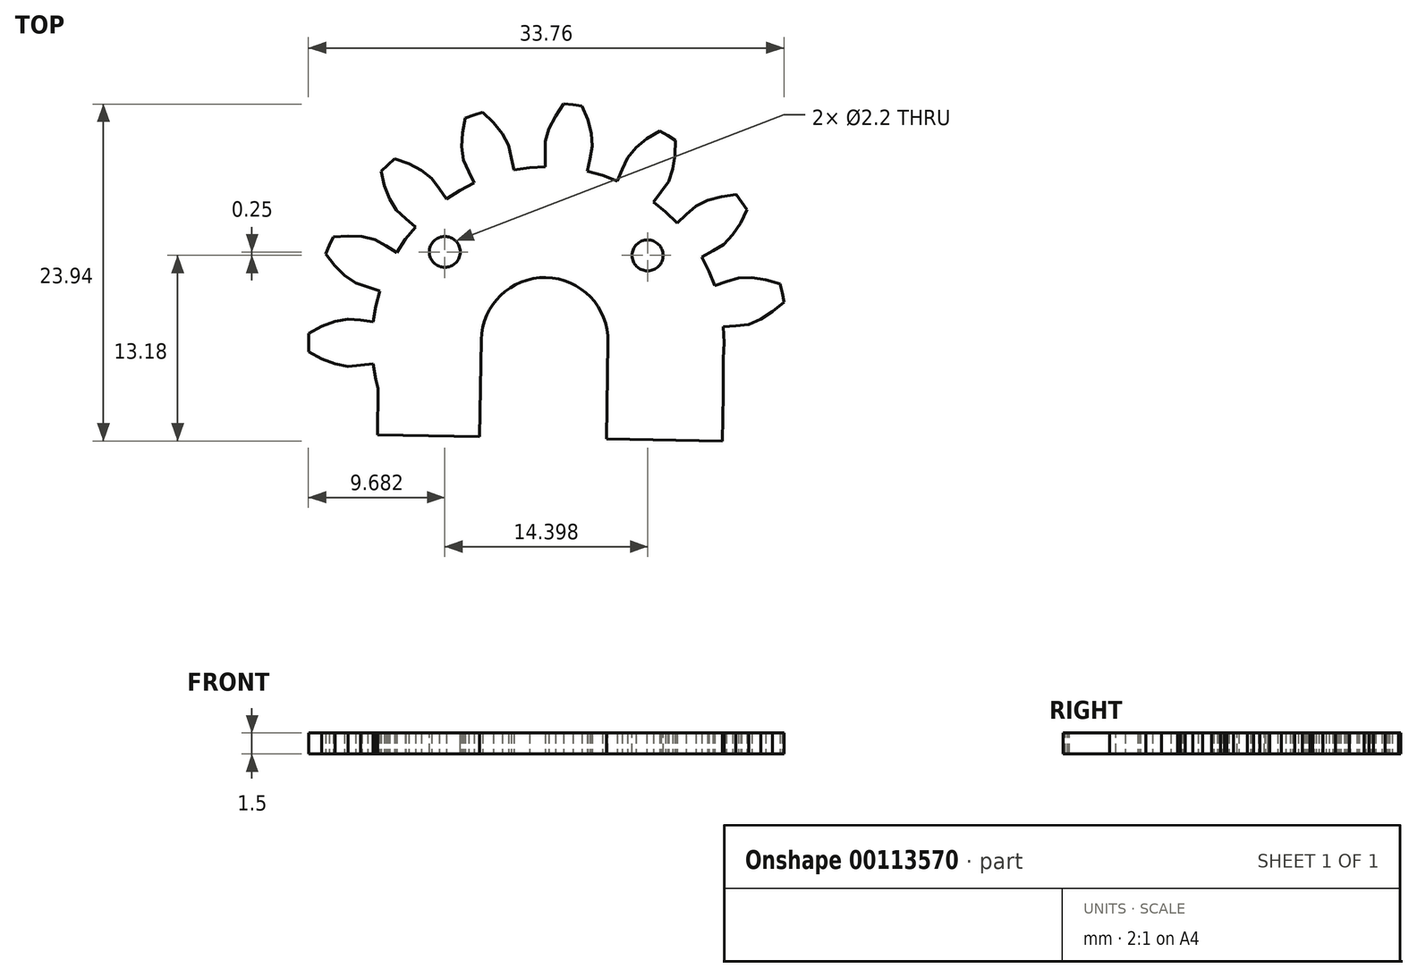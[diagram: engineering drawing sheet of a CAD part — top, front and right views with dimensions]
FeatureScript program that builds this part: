
annotation { "Feature Type Name" : "Feature", "Feature Type Description" : "" }
export const myFeature = defineFeature(function(context is Context, id is Id, definition is map)
    precondition{}
    {
        {
            var Q0;
            Q0=qCreatedBy(makeId("Top.planeOp"),FACE);
            var sketch = newSketch(context, id + "F0", { "sketchPlane" : qUnion([Q0])});
            skLineSegment(sketch, "E0", {"start": v(12.62, 0) * mm, "end": v(12.57, 1.12) * mm});
            skLineSegment(sketch, "E1", {"start": v(12.57, 1.12) * mm, "end": v(13.47, 1.2) * mm});
            skLineSegment(sketch, "E2", {"start": v(13.47, 1.2) * mm, "end": v(14.36, 1.3) * mm});
            skLineSegment(sketch, "E3", {"start": v(14.36, 1.3) * mm, "end": v(15.23, 1.67) * mm});
            skLineSegment(sketch, "E4", {"start": v(15.23, 1.67) * mm, "end": v(16.07, 2.2) * mm});
            skLineSegment(sketch, "E5", {"start": v(16.07, 2.2) * mm, "end": v(16.88, 2.89) * mm});
            skLineSegment(sketch, "E6", {"start": v(16.88, 2.89) * mm, "end": v(16.75, 3.53) * mm});
            skLineSegment(sketch, "E7", {"start": v(16.75, 3.53) * mm, "end": v(16.6, 4.17) * mm});
            skLineSegment(sketch, "E8", {"start": v(16.6, 4.17) * mm, "end": v(15.6, 4.47) * mm});
            skLineSegment(sketch, "E9", {"start": v(15.6, 4.47) * mm, "end": v(14.6, 4.62) * mm});
            skLineSegment(sketch, "E10", {"start": v(14.6, 4.62) * mm, "end": v(13.66, 4.6) * mm});
            skLineSegment(sketch, "E11", {"start": v(13.66, 4.6) * mm, "end": v(12.8, 4.33) * mm});
            skLineSegment(sketch, "E12", {"start": v(12.8, 4.33) * mm, "end": v(11.95, 4.04) * mm});
            skLineSegment(sketch, "E13", {"start": v(11.95, 4.04) * mm, "end": v(11.54, 5.08) * mm});
            skLineSegment(sketch, "E14", {"start": v(11.54, 5.08) * mm, "end": v(11.04, 6.09) * mm});
            skLineSegment(sketch, "E15", {"start": v(11.04, 6.09) * mm, "end": v(11.83, 6.53) * mm});
            skLineSegment(sketch, "E16", {"start": v(11.83, 6.53) * mm, "end": v(12.6, 6.99) * mm});
            skLineSegment(sketch, "E17", {"start": v(12.6, 6.99) * mm, "end": v(13.25, 7.67) * mm});
            skLineSegment(sketch, "E18", {"start": v(13.25, 7.67) * mm, "end": v(13.8, 8.5) * mm});
            skLineSegment(sketch, "E19", {"start": v(13.8, 8.5) * mm, "end": v(14.25, 9.45) * mm});
            skLineSegment(sketch, "E20", {"start": v(14.25, 9.45) * mm, "end": v(13.88, 10) * mm});
            skLineSegment(sketch, "E21", {"start": v(13.88, 10) * mm, "end": v(13.48, 10.52) * mm});
            skLineSegment(sketch, "E22", {"start": v(13.48, 10.52) * mm, "end": v(12.43, 10.38) * mm});
            skLineSegment(sketch, "E23", {"start": v(12.43, 10.38) * mm, "end": v(11.47, 10.11) * mm});
            skLineSegment(sketch, "E24", {"start": v(11.47, 10.11) * mm, "end": v(10.62, 9.7) * mm});
            skLineSegment(sketch, "E25", {"start": v(10.62, 9.7) * mm, "end": v(9.95, 9.11) * mm});
            skLineSegment(sketch, "E26", {"start": v(9.95, 9.11) * mm, "end": v(9.29, 8.5) * mm});
            skLineSegment(sketch, "E27", {"start": v(9.29, 8.5) * mm, "end": v(8.49, 9.29) * mm});
            skLineSegment(sketch, "E28", {"start": v(8.49, 9.29) * mm, "end": v(7.62, 10) * mm});
            skLineSegment(sketch, "E29", {"start": v(7.62, 10) * mm, "end": v(8.16, 10.72) * mm});
            skLineSegment(sketch, "E30", {"start": v(8.16, 10.72) * mm, "end": v(8.68, 11.46) * mm});
            skLineSegment(sketch, "E31", {"start": v(8.68, 11.46) * mm, "end": v(9, 12.34) * mm});
            skLineSegment(sketch, "E32", {"start": v(9, 12.34) * mm, "end": v(9.16, 13.33) * mm});
            skLineSegment(sketch, "E33", {"start": v(9.16, 13.33) * mm, "end": v(9.19, 14.38) * mm});
            skLineSegment(sketch, "E34", {"start": v(9.19, 14.38) * mm, "end": v(8.62, 14.72) * mm});
            skLineSegment(sketch, "E35", {"start": v(8.62, 14.72) * mm, "end": v(8.05, 15.04) * mm});
            skLineSegment(sketch, "E36", {"start": v(8.05, 15.04) * mm, "end": v(7.15, 14.49) * mm});
            skLineSegment(sketch, "E37", {"start": v(7.15, 14.49) * mm, "end": v(6.38, 13.85) * mm});
            skLineSegment(sketch, "E38", {"start": v(6.38, 13.85) * mm, "end": v(5.77, 13.14) * mm});
            skLineSegment(sketch, "E39", {"start": v(5.77, 13.14) * mm, "end": v(5.4, 12.32) * mm});
            skLineSegment(sketch, "E40", {"start": v(5.4, 12.32) * mm, "end": v(5.04, 11.5) * mm});
            skLineSegment(sketch, "E41", {"start": v(5.04, 11.5) * mm, "end": v(3.99, 11.89) * mm});
            skLineSegment(sketch, "E42", {"start": v(3.99, 11.89) * mm, "end": v(2.9, 12.19) * mm});
            skLineSegment(sketch, "E43", {"start": v(2.9, 12.19) * mm, "end": v(3.1, 13.06) * mm});
            skLineSegment(sketch, "E44", {"start": v(3.1, 13.06) * mm, "end": v(3.28, 13.95) * mm});
            skLineSegment(sketch, "E45", {"start": v(3.28, 13.95) * mm, "end": v(3.2, 14.88) * mm});
            skLineSegment(sketch, "E46", {"start": v(3.2, 14.88) * mm, "end": v(2.95, 15.85) * mm});
            skLineSegment(sketch, "E47", {"start": v(2.95, 15.85) * mm, "end": v(2.55, 16.83) * mm});
            skLineSegment(sketch, "E48", {"start": v(2.55, 16.83) * mm, "end": v(1.9, 16.9) * mm});
            skLineSegment(sketch, "E49", {"start": v(1.9, 16.9) * mm, "end": v(1.25, 16.96) * mm});
            skLineSegment(sketch, "E50", {"start": v(1.25, 16.96) * mm, "end": v(0.65, 16.1) * mm});
            skLineSegment(sketch, "E51", {"start": v(0.65, 16.1) * mm, "end": v(0.2, 15.2) * mm});
            skLineSegment(sketch, "E52", {"start": v(0.2, 15.2) * mm, "end": v(-0.07, 14.3) * mm});
            skLineSegment(sketch, "E53", {"start": v(-0.07, 14.3) * mm, "end": v(-0.08, 13.4) * mm});
            skLineSegment(sketch, "E54", {"start": v(-0.08, 13.4) * mm, "end": v(-0.06, 12.5) * mm});
            skLineSegment(sketch, "E55", {"start": v(-0.06, 12.5) * mm, "end": v(-1.18, 12.43) * mm});
            skLineSegment(sketch, "E56", {"start": v(-1.18, 12.43) * mm, "end": v(-2.3, 12.26) * mm});
            skLineSegment(sketch, "E57", {"start": v(-2.3, 12.26) * mm, "end": v(-2.47, 13.15) * mm});
            skLineSegment(sketch, "E58", {"start": v(-2.47, 13.15) * mm, "end": v(-2.66, 14.03) * mm});
            skLineSegment(sketch, "E59", {"start": v(-2.66, 14.03) * mm, "end": v(-3.11, 14.85) * mm});
            skLineSegment(sketch, "E60", {"start": v(-3.11, 14.85) * mm, "end": v(-3.74, 15.63) * mm});
            skLineSegment(sketch, "E61", {"start": v(-3.74, 15.63) * mm, "end": v(-4.5, 16.36) * mm});
            skLineSegment(sketch, "E62", {"start": v(-4.5, 16.36) * mm, "end": v(-5.13, 16.17) * mm});
            skLineSegment(sketch, "E63", {"start": v(-5.13, 16.17) * mm, "end": v(-5.75, 15.95) * mm});
            skLineSegment(sketch, "E64", {"start": v(-5.75, 15.95) * mm, "end": v(-5.94, 14.91) * mm});
            skLineSegment(sketch, "E65", {"start": v(-5.94, 14.91) * mm, "end": v(-5.99, 13.92) * mm});
            skLineSegment(sketch, "E66", {"start": v(-5.99, 13.92) * mm, "end": v(-5.87, 12.99) * mm});
            skLineSegment(sketch, "E67", {"start": v(-5.87, 12.99) * mm, "end": v(-5.5, 12.16) * mm});
            skLineSegment(sketch, "E68", {"start": v(-5.5, 12.16) * mm, "end": v(-5.13, 11.34) * mm});
            skLineSegment(sketch, "E69", {"start": v(-5.13, 11.34) * mm, "end": v(-6.13, 10.83) * mm});
            skLineSegment(sketch, "E70", {"start": v(-6.13, 10.83) * mm, "end": v(-7.07, 10.22) * mm});
            skLineSegment(sketch, "E71", {"start": v(-7.07, 10.22) * mm, "end": v(-7.6, 10.96) * mm});
            skLineSegment(sketch, "E72", {"start": v(-7.6, 10.96) * mm, "end": v(-8.13, 11.68) * mm});
            skLineSegment(sketch, "E73", {"start": v(-8.13, 11.68) * mm, "end": v(-8.87, 12.25) * mm});
            skLineSegment(sketch, "E74", {"start": v(-8.87, 12.25) * mm, "end": v(-9.76, 12.7) * mm});
            skLineSegment(sketch, "E75", {"start": v(-9.76, 12.7) * mm, "end": v(-10.76, 13.06) * mm});
            skLineSegment(sketch, "E76", {"start": v(-10.76, 13.06) * mm, "end": v(-11.25, 12.63) * mm});
            skLineSegment(sketch, "E77", {"start": v(-11.25, 12.63) * mm, "end": v(-11.73, 12.18) * mm});
            skLineSegment(sketch, "E78", {"start": v(-11.73, 12.18) * mm, "end": v(-11.48, 11.16) * mm});
            skLineSegment(sketch, "E79", {"start": v(-11.48, 11.16) * mm, "end": v(-11.12, 10.23) * mm});
            skLineSegment(sketch, "E80", {"start": v(-11.12, 10.23) * mm, "end": v(-10.63, 9.43) * mm});
            skLineSegment(sketch, "E81", {"start": v(-10.63, 9.43) * mm, "end": v(-9.97, 8.82) * mm});
            skLineSegment(sketch, "E82", {"start": v(-9.97, 8.82) * mm, "end": v(-9.29, 8.22) * mm});
            skLineSegment(sketch, "E83", {"start": v(-9.29, 8.22) * mm, "end": v(-9.99, 7.35) * mm});
            skLineSegment(sketch, "E84", {"start": v(-9.99, 7.35) * mm, "end": v(-10.6, 6.41) * mm});
            skLineSegment(sketch, "E85", {"start": v(-10.6, 6.41) * mm, "end": v(-11.38, 6.87) * mm});
            skLineSegment(sketch, "E86", {"start": v(-11.38, 6.87) * mm, "end": v(-12.16, 7.31) * mm});
            skLineSegment(sketch, "E87", {"start": v(-12.16, 7.31) * mm, "end": v(-13.08, 7.53) * mm});
            skLineSegment(sketch, "E88", {"start": v(-13.08, 7.53) * mm, "end": v(-14.08, 7.59) * mm});
            skLineSegment(sketch, "E89", {"start": v(-14.08, 7.59) * mm, "end": v(-15.13, 7.5) * mm});
            skLineSegment(sketch, "E90", {"start": v(-15.13, 7.5) * mm, "end": v(-15.4, 6.91) * mm});
            skLineSegment(sketch, "E91", {"start": v(-15.4, 6.91) * mm, "end": v(-15.66, 6.3) * mm});
            skLineSegment(sketch, "E92", {"start": v(-15.66, 6.3) * mm, "end": v(-15.02, 5.47) * mm});
            skLineSegment(sketch, "E93", {"start": v(-15.02, 5.47) * mm, "end": v(-14.3, 4.77) * mm});
            skLineSegment(sketch, "E94", {"start": v(-14.3, 4.77) * mm, "end": v(-13.53, 4.24) * mm});
            skLineSegment(sketch, "E95", {"start": v(-13.53, 4.24) * mm, "end": v(-12.68, 3.95) * mm});
            skLineSegment(sketch, "E96", {"start": v(-12.68, 3.95) * mm, "end": v(-11.82, 3.69) * mm});
            skLineSegment(sketch, "E97", {"start": v(-11.82, 3.69) * mm, "end": v(-12.1, 2.6) * mm});
            skLineSegment(sketch, "E98", {"start": v(-12.1, 2.6) * mm, "end": v(-12.29, 1.5) * mm});
            skLineSegment(sketch, "E99", {"start": v(-12.29, 1.5) * mm, "end": v(-13.18, 1.6) * mm});
            skLineSegment(sketch, "E100", {"start": v(-13.18, 1.6) * mm, "end": v(-14.08, 1.68) * mm});
            skLineSegment(sketch, "E101", {"start": v(-14.08, 1.68) * mm, "end": v(-15, 1.51) * mm});
            skLineSegment(sketch, "E102", {"start": v(-15, 1.51) * mm, "end": v(-15.93, 1.16) * mm});
            skLineSegment(sketch, "E103", {"start": v(-15.93, 1.16) * mm, "end": v(-16.86, 0.66) * mm});
            skLineSegment(sketch, "E104", {"start": v(-16.86, 0.66) * mm, "end": v(-16.88, 0) * mm});
            skLineSegment(sketch, "E105", {"start": v(-16.88, 0) * mm, "end": v(-16.86, -0.66) * mm});
            skLineSegment(sketch, "E106", {"start": v(-16.86, -0.66) * mm, "end": v(-15.93, -1.16) * mm});
            skLineSegment(sketch, "E107", {"start": v(-15.93, -1.16) * mm, "end": v(-15, -1.51) * mm});
            skLineSegment(sketch, "E108", {"start": v(-15, -1.51) * mm, "end": v(-14.08, -1.68) * mm});
            skLineSegment(sketch, "E109", {"start": v(-14.08, -1.68) * mm, "end": v(-13.18, -1.6) * mm});
            skLineSegment(sketch, "E110", {"start": v(-13.18, -1.6) * mm, "end": v(-12.29, -1.5) * mm});
            skLineSegment(sketch, "E111", {"start": v(-12.29, -1.5) * mm, "end": v(-12.1, -2.6) * mm});
            skLineSegment(sketch, "E112", {"start": v(-12.1, -2.6) * mm, "end": v(-11.82, -3.69) * mm});
            skLineSegment(sketch, "E113", {"start": v(-11.82, -3.69) * mm, "end": v(-12.68, -3.95) * mm});
            skLineSegment(sketch, "E114", {"start": v(-12.68, -3.95) * mm, "end": v(-13.53, -4.24) * mm});
            skLineSegment(sketch, "E115", {"start": v(-13.53, -4.24) * mm, "end": v(-14.3, -4.77) * mm});
            skLineSegment(sketch, "E116", {"start": v(-14.3, -4.77) * mm, "end": v(-15.02, -5.47) * mm});
            skLineSegment(sketch, "E117", {"start": v(-15.02, -5.47) * mm, "end": v(-15.66, -6.3) * mm});
            skLineSegment(sketch, "E118", {"start": v(-15.66, -6.3) * mm, "end": v(-15.4, -6.91) * mm});
            skLineSegment(sketch, "E119", {"start": v(-15.4, -6.91) * mm, "end": v(-15.13, -7.5) * mm});
            skLineSegment(sketch, "E120", {"start": v(-15.13, -7.5) * mm, "end": v(-14.08, -7.59) * mm});
            skLineSegment(sketch, "E121", {"start": v(-14.08, -7.59) * mm, "end": v(-13.08, -7.53) * mm});
            skLineSegment(sketch, "E122", {"start": v(-13.08, -7.53) * mm, "end": v(-12.16, -7.31) * mm});
            skLineSegment(sketch, "E123", {"start": v(-12.16, -7.31) * mm, "end": v(-11.38, -6.87) * mm});
            skLineSegment(sketch, "E124", {"start": v(-11.38, -6.87) * mm, "end": v(-10.6, -6.41) * mm});
            skLineSegment(sketch, "E125", {"start": v(-10.6, -6.41) * mm, "end": v(-9.99, -7.35) * mm});
            skLineSegment(sketch, "E126", {"start": v(-9.99, -7.35) * mm, "end": v(-9.29, -8.22) * mm});
            skLineSegment(sketch, "E127", {"start": v(-9.29, -8.22) * mm, "end": v(-9.97, -8.82) * mm});
            skLineSegment(sketch, "E128", {"start": v(-9.97, -8.82) * mm, "end": v(-10.63, -9.43) * mm});
            skLineSegment(sketch, "E129", {"start": v(-10.63, -9.43) * mm, "end": v(-11.12, -10.23) * mm});
            skLineSegment(sketch, "E130", {"start": v(-11.12, -10.23) * mm, "end": v(-11.48, -11.16) * mm});
            skLineSegment(sketch, "E131", {"start": v(-11.48, -11.16) * mm, "end": v(-11.73, -12.18) * mm});
            skLineSegment(sketch, "E132", {"start": v(-11.73, -12.18) * mm, "end": v(-11.25, -12.63) * mm});
            skLineSegment(sketch, "E133", {"start": v(-11.25, -12.63) * mm, "end": v(-10.76, -13.06) * mm});
            skLineSegment(sketch, "E134", {"start": v(-10.76, -13.06) * mm, "end": v(-9.76, -12.7) * mm});
            skLineSegment(sketch, "E135", {"start": v(-9.76, -12.7) * mm, "end": v(-8.87, -12.25) * mm});
            skLineSegment(sketch, "E136", {"start": v(-8.87, -12.25) * mm, "end": v(-8.13, -11.68) * mm});
            skLineSegment(sketch, "E137", {"start": v(-8.13, -11.68) * mm, "end": v(-7.6, -10.96) * mm});
            skLineSegment(sketch, "E138", {"start": v(-7.6, -10.96) * mm, "end": v(-7.07, -10.22) * mm});
            skLineSegment(sketch, "E139", {"start": v(-7.07, -10.22) * mm, "end": v(-6.13, -10.83) * mm});
            skLineSegment(sketch, "E140", {"start": v(-6.13, -10.83) * mm, "end": v(-5.13, -11.34) * mm});
            skLineSegment(sketch, "E141", {"start": v(-5.13, -11.34) * mm, "end": v(-5.5, -12.16) * mm});
            skLineSegment(sketch, "E142", {"start": v(-5.5, -12.16) * mm, "end": v(-5.87, -12.99) * mm});
            skLineSegment(sketch, "E143", {"start": v(-5.87, -12.99) * mm, "end": v(-5.99, -13.92) * mm});
            skLineSegment(sketch, "E144", {"start": v(-5.99, -13.92) * mm, "end": v(-5.94, -14.91) * mm});
            skLineSegment(sketch, "E145", {"start": v(-5.94, -14.91) * mm, "end": v(-5.75, -15.95) * mm});
            skLineSegment(sketch, "E146", {"start": v(-5.75, -15.95) * mm, "end": v(-5.13, -16.17) * mm});
            skLineSegment(sketch, "E147", {"start": v(-5.13, -16.17) * mm, "end": v(-4.5, -16.36) * mm});
            skLineSegment(sketch, "E148", {"start": v(-4.5, -16.36) * mm, "end": v(-3.74, -15.63) * mm});
            skLineSegment(sketch, "E149", {"start": v(-3.74, -15.63) * mm, "end": v(-3.11, -14.85) * mm});
            skLineSegment(sketch, "E150", {"start": v(-3.11, -14.85) * mm, "end": v(-2.66, -14.03) * mm});
            skLineSegment(sketch, "E151", {"start": v(-2.66, -14.03) * mm, "end": v(-2.47, -13.15) * mm});
            skLineSegment(sketch, "E152", {"start": v(-2.47, -13.15) * mm, "end": v(-2.3, -12.26) * mm});
            skLineSegment(sketch, "E153", {"start": v(-2.3, -12.26) * mm, "end": v(-1.18, -12.43) * mm});
            skLineSegment(sketch, "E154", {"start": v(-1.18, -12.43) * mm, "end": v(-0.06, -12.5) * mm});
            skLineSegment(sketch, "E155", {"start": v(-0.06, -12.5) * mm, "end": v(-0.08, -13.4) * mm});
            skLineSegment(sketch, "E156", {"start": v(-0.08, -13.4) * mm, "end": v(-0.07, -14.3) * mm});
            skLineSegment(sketch, "E157", {"start": v(-0.07, -14.3) * mm, "end": v(0.2, -15.2) * mm});
            skLineSegment(sketch, "E158", {"start": v(0.2, -15.2) * mm, "end": v(0.65, -16.1) * mm});
            skLineSegment(sketch, "E159", {"start": v(0.65, -16.1) * mm, "end": v(1.25, -16.96) * mm});
            skLineSegment(sketch, "E160", {"start": v(1.25, -16.96) * mm, "end": v(1.9, -16.9) * mm});
            skLineSegment(sketch, "E161", {"start": v(1.9, -16.9) * mm, "end": v(2.55, -16.83) * mm});
            skLineSegment(sketch, "E162", {"start": v(2.55, -16.83) * mm, "end": v(2.95, -15.85) * mm});
            skLineSegment(sketch, "E163", {"start": v(2.95, -15.85) * mm, "end": v(3.2, -14.88) * mm});
            skLineSegment(sketch, "E164", {"start": v(3.2, -14.88) * mm, "end": v(3.28, -13.95) * mm});
            skLineSegment(sketch, "E165", {"start": v(3.28, -13.95) * mm, "end": v(3.1, -13.06) * mm});
            skLineSegment(sketch, "E166", {"start": v(3.1, -13.06) * mm, "end": v(2.9, -12.19) * mm});
            skLineSegment(sketch, "E167", {"start": v(2.9, -12.19) * mm, "end": v(3.99, -11.89) * mm});
            skLineSegment(sketch, "E168", {"start": v(3.99, -11.89) * mm, "end": v(5.04, -11.5) * mm});
            skLineSegment(sketch, "E169", {"start": v(5.04, -11.5) * mm, "end": v(5.4, -12.32) * mm});
            skLineSegment(sketch, "E170", {"start": v(5.4, -12.32) * mm, "end": v(5.77, -13.14) * mm});
            skLineSegment(sketch, "E171", {"start": v(5.77, -13.14) * mm, "end": v(6.38, -13.85) * mm});
            skLineSegment(sketch, "E172", {"start": v(6.38, -13.85) * mm, "end": v(7.15, -14.49) * mm});
            skLineSegment(sketch, "E173", {"start": v(7.15, -14.49) * mm, "end": v(8.05, -15.04) * mm});
            skLineSegment(sketch, "E174", {"start": v(8.05, -15.04) * mm, "end": v(8.62, -14.72) * mm});
            skLineSegment(sketch, "E175", {"start": v(8.62, -14.72) * mm, "end": v(9.19, -14.38) * mm});
            skLineSegment(sketch, "E176", {"start": v(9.19, -14.38) * mm, "end": v(9.16, -13.33) * mm});
            skLineSegment(sketch, "E177", {"start": v(9.16, -13.33) * mm, "end": v(9, -12.34) * mm});
            skLineSegment(sketch, "E178", {"start": v(9, -12.34) * mm, "end": v(8.68, -11.46) * mm});
            skLineSegment(sketch, "E179", {"start": v(8.68, -11.46) * mm, "end": v(8.16, -10.72) * mm});
            skLineSegment(sketch, "E180", {"start": v(8.16, -10.72) * mm, "end": v(7.62, -10) * mm});
            skLineSegment(sketch, "E181", {"start": v(7.62, -10) * mm, "end": v(8.49, -9.29) * mm});
            skLineSegment(sketch, "E182", {"start": v(8.49, -9.29) * mm, "end": v(9.29, -8.5) * mm});
            skLineSegment(sketch, "E183", {"start": v(9.29, -8.5) * mm, "end": v(9.95, -9.11) * mm});
            skLineSegment(sketch, "E184", {"start": v(9.95, -9.11) * mm, "end": v(10.62, -9.7) * mm});
            skLineSegment(sketch, "E185", {"start": v(10.62, -9.7) * mm, "end": v(11.47, -10.11) * mm});
            skLineSegment(sketch, "E186", {"start": v(11.47, -10.11) * mm, "end": v(12.43, -10.38) * mm});
            skLineSegment(sketch, "E187", {"start": v(12.43, -10.38) * mm, "end": v(13.48, -10.52) * mm});
            skLineSegment(sketch, "E188", {"start": v(13.48, -10.52) * mm, "end": v(13.88, -10) * mm});
            skLineSegment(sketch, "E189", {"start": v(13.88, -10) * mm, "end": v(14.25, -9.45) * mm});
            skLineSegment(sketch, "E190", {"start": v(14.25, -9.45) * mm, "end": v(13.8, -8.5) * mm});
            skLineSegment(sketch, "E191", {"start": v(13.8, -8.5) * mm, "end": v(13.25, -7.67) * mm});
            skLineSegment(sketch, "E192", {"start": v(13.25, -7.67) * mm, "end": v(12.6, -6.99) * mm});
            skLineSegment(sketch, "E193", {"start": v(12.6, -6.99) * mm, "end": v(11.83, -6.53) * mm});
            skLineSegment(sketch, "E194", {"start": v(11.83, -6.53) * mm, "end": v(11.04, -6.09) * mm});
            skLineSegment(sketch, "E195", {"start": v(11.04, -6.09) * mm, "end": v(11.54, -5.08) * mm});
            skLineSegment(sketch, "E196", {"start": v(11.54, -5.08) * mm, "end": v(11.95, -4.04) * mm});
            skLineSegment(sketch, "E197", {"start": v(11.95, -4.04) * mm, "end": v(12.8, -4.33) * mm});
            skLineSegment(sketch, "E198", {"start": v(12.8, -4.33) * mm, "end": v(13.66, -4.6) * mm});
            skLineSegment(sketch, "E199", {"start": v(13.66, -4.6) * mm, "end": v(14.6, -4.62) * mm});
            skLineSegment(sketch, "E200", {"start": v(14.6, -4.62) * mm, "end": v(15.6, -4.47) * mm});
            skLineSegment(sketch, "E201", {"start": v(15.6, -4.47) * mm, "end": v(16.6, -4.17) * mm});
            skLineSegment(sketch, "E202", {"start": v(16.6, -4.17) * mm, "end": v(16.75, -3.53) * mm});
            skLineSegment(sketch, "E203", {"start": v(16.75, -3.53) * mm, "end": v(16.88, -2.89) * mm});
            skLineSegment(sketch, "E204", {"start": v(16.88, -2.89) * mm, "end": v(16.07, -2.2) * mm});
            skLineSegment(sketch, "E205", {"start": v(16.07, -2.2) * mm, "end": v(15.23, -1.67) * mm});
            skLineSegment(sketch, "E206", {"start": v(15.23, -1.67) * mm, "end": v(14.36, -1.3) * mm});
            skLineSegment(sketch, "E207", {"start": v(14.36, -1.3) * mm, "end": v(13.47, -1.2) * mm});
            skLineSegment(sketch, "E208", {"start": v(13.47, -1.2) * mm, "end": v(12.57, -1.12) * mm});
            skLineSegment(sketch, "E209", {"start": v(12.62, 0) * mm, "end": v(12.57, -1.12) * mm});
            skSolve(sketch);
        }
        {
            var Q0;
            Q0 = qSketchRegion(id + "F0", true);
            extrude(context, id + "F1", {"entities" : qUnion([Q0]), "depth" : 1.5 * mm});
        }
        {
            var Q0;
            Q0=makeQuery(id+"F1.opExtrude","CAP_FACE",FACE,{"disambiguationData":[OSD([sQuery(id+"F0.wireOp",EDGE,"E0"),sQuery(id+"F0.wireOp",EDGE,"E1"),sQuery(id+"F0.wireOp",EDGE,"E2"),sQuery(id+"F0.wireOp",EDGE,"E3"),sQuery(id+"F0.wireOp",EDGE,"E4"),sQuery(id+"F0.wireOp",EDGE,"E5"),sQuery(id+"F0.wireOp",EDGE,"E6"),sQuery(id+"F0.wireOp",EDGE,"E7"),sQuery(id+"F0.wireOp",EDGE,"E8"),sQuery(id+"F0.wireOp",EDGE,"E9"),sQuery(id+"F0.wireOp",EDGE,"E10"),sQuery(id+"F0.wireOp",EDGE,"E11"),sQuery(id+"F0.wireOp",EDGE,"E12"),sQuery(id+"F0.wireOp",EDGE,"E13"),sQuery(id+"F0.wireOp",EDGE,"E14"),sQuery(id+"F0.wireOp",EDGE,"E15"),sQuery(id+"F0.wireOp",EDGE,"E16"),sQuery(id+"F0.wireOp",EDGE,"E17"),sQuery(id+"F0.wireOp",EDGE,"E18"),sQuery(id+"F0.wireOp",EDGE,"E19"),sQuery(id+"F0.wireOp",EDGE,"E20"),sQuery(id+"F0.wireOp",EDGE,"E21"),sQuery(id+"F0.wireOp",EDGE,"E22"),sQuery(id+"F0.wireOp",EDGE,"E23"),sQuery(id+"F0.wireOp",EDGE,"E24"),sQuery(id+"F0.wireOp",EDGE,"E25"),sQuery(id+"F0.wireOp",EDGE,"E26"),sQuery(id+"F0.wireOp",EDGE,"E27"),sQuery(id+"F0.wireOp",EDGE,"E28"),sQuery(id+"F0.wireOp",EDGE,"E29"),sQuery(id+"F0.wireOp",EDGE,"E30"),sQuery(id+"F0.wireOp",EDGE,"E31"),sQuery(id+"F0.wireOp",EDGE,"E32"),sQuery(id+"F0.wireOp",EDGE,"E33"),sQuery(id+"F0.wireOp",EDGE,"E34"),sQuery(id+"F0.wireOp",EDGE,"E35"),sQuery(id+"F0.wireOp",EDGE,"E36"),sQuery(id+"F0.wireOp",EDGE,"E37"),sQuery(id+"F0.wireOp",EDGE,"E38"),sQuery(id+"F0.wireOp",EDGE,"E39"),sQuery(id+"F0.wireOp",EDGE,"E40"),sQuery(id+"F0.wireOp",EDGE,"E41"),sQuery(id+"F0.wireOp",EDGE,"E42"),sQuery(id+"F0.wireOp",EDGE,"E43"),sQuery(id+"F0.wireOp",EDGE,"E44"),sQuery(id+"F0.wireOp",EDGE,"E45"),sQuery(id+"F0.wireOp",EDGE,"E46"),sQuery(id+"F0.wireOp",EDGE,"E47"),sQuery(id+"F0.wireOp",EDGE,"E48"),sQuery(id+"F0.wireOp",EDGE,"E49"),sQuery(id+"F0.wireOp",EDGE,"E50"),sQuery(id+"F0.wireOp",EDGE,"E51"),sQuery(id+"F0.wireOp",EDGE,"E52"),sQuery(id+"F0.wireOp",EDGE,"E53"),sQuery(id+"F0.wireOp",EDGE,"E54"),sQuery(id+"F0.wireOp",EDGE,"E55"),sQuery(id+"F0.wireOp",EDGE,"E56"),sQuery(id+"F0.wireOp",EDGE,"E57"),sQuery(id+"F0.wireOp",EDGE,"E58"),sQuery(id+"F0.wireOp",EDGE,"E59"),sQuery(id+"F0.wireOp",EDGE,"E60"),sQuery(id+"F0.wireOp",EDGE,"E61"),sQuery(id+"F0.wireOp",EDGE,"E62"),sQuery(id+"F0.wireOp",EDGE,"E63"),sQuery(id+"F0.wireOp",EDGE,"E64"),sQuery(id+"F0.wireOp",EDGE,"E65"),sQuery(id+"F0.wireOp",EDGE,"E66"),sQuery(id+"F0.wireOp",EDGE,"E67"),sQuery(id+"F0.wireOp",EDGE,"E68"),sQuery(id+"F0.wireOp",EDGE,"E69"),sQuery(id+"F0.wireOp",EDGE,"E70"),sQuery(id+"F0.wireOp",EDGE,"E71"),sQuery(id+"F0.wireOp",EDGE,"E72"),sQuery(id+"F0.wireOp",EDGE,"E73"),sQuery(id+"F0.wireOp",EDGE,"E74"),sQuery(id+"F0.wireOp",EDGE,"E75"),sQuery(id+"F0.wireOp",EDGE,"E76"),sQuery(id+"F0.wireOp",EDGE,"E77"),sQuery(id+"F0.wireOp",EDGE,"E78"),sQuery(id+"F0.wireOp",EDGE,"E79"),sQuery(id+"F0.wireOp",EDGE,"E80"),sQuery(id+"F0.wireOp",EDGE,"E81"),sQuery(id+"F0.wireOp",EDGE,"E82"),sQuery(id+"F0.wireOp",EDGE,"E83"),sQuery(id+"F0.wireOp",EDGE,"E84"),sQuery(id+"F0.wireOp",EDGE,"E85"),sQuery(id+"F0.wireOp",EDGE,"E86"),sQuery(id+"F0.wireOp",EDGE,"E87"),sQuery(id+"F0.wireOp",EDGE,"E88"),sQuery(id+"F0.wireOp",EDGE,"E89"),sQuery(id+"F0.wireOp",EDGE,"E90"),sQuery(id+"F0.wireOp",EDGE,"E91"),sQuery(id+"F0.wireOp",EDGE,"E92"),sQuery(id+"F0.wireOp",EDGE,"E93"),sQuery(id+"F0.wireOp",EDGE,"E94"),sQuery(id+"F0.wireOp",EDGE,"E95"),sQuery(id+"F0.wireOp",EDGE,"E96"),sQuery(id+"F0.wireOp",EDGE,"E97"),sQuery(id+"F0.wireOp",EDGE,"E98"),sQuery(id+"F0.wireOp",EDGE,"E99"),sQuery(id+"F0.wireOp",EDGE,"E100"),sQuery(id+"F0.wireOp",EDGE,"E101"),sQuery(id+"F0.wireOp",EDGE,"E102"),sQuery(id+"F0.wireOp",EDGE,"E103"),sQuery(id+"F0.wireOp",EDGE,"E104"),sQuery(id+"F0.wireOp",EDGE,"E105"),sQuery(id+"F0.wireOp",EDGE,"E106"),sQuery(id+"F0.wireOp",EDGE,"E107"),sQuery(id+"F0.wireOp",EDGE,"E108"),sQuery(id+"F0.wireOp",EDGE,"E109"),sQuery(id+"F0.wireOp",EDGE,"E110"),sQuery(id+"F0.wireOp",EDGE,"E111"),sQuery(id+"F0.wireOp",EDGE,"E112"),sQuery(id+"F0.wireOp",EDGE,"E113"),sQuery(id+"F0.wireOp",EDGE,"E114"),sQuery(id+"F0.wireOp",EDGE,"E115"),sQuery(id+"F0.wireOp",EDGE,"E116"),sQuery(id+"F0.wireOp",EDGE,"E117"),sQuery(id+"F0.wireOp",EDGE,"E118"),sQuery(id+"F0.wireOp",EDGE,"E119"),sQuery(id+"F0.wireOp",EDGE,"E120"),sQuery(id+"F0.wireOp",EDGE,"E121"),sQuery(id+"F0.wireOp",EDGE,"E122"),sQuery(id+"F0.wireOp",EDGE,"E123"),sQuery(id+"F0.wireOp",EDGE,"E124"),sQuery(id+"F0.wireOp",EDGE,"E125"),sQuery(id+"F0.wireOp",EDGE,"E126"),sQuery(id+"F0.wireOp",EDGE,"E127"),sQuery(id+"F0.wireOp",EDGE,"E128"),sQuery(id+"F0.wireOp",EDGE,"E129"),sQuery(id+"F0.wireOp",EDGE,"E130"),sQuery(id+"F0.wireOp",EDGE,"E131"),sQuery(id+"F0.wireOp",EDGE,"E132"),sQuery(id+"F0.wireOp",EDGE,"E133"),sQuery(id+"F0.wireOp",EDGE,"E134"),sQuery(id+"F0.wireOp",EDGE,"E135"),sQuery(id+"F0.wireOp",EDGE,"E136"),sQuery(id+"F0.wireOp",EDGE,"E137"),sQuery(id+"F0.wireOp",EDGE,"E138"),sQuery(id+"F0.wireOp",EDGE,"E139"),sQuery(id+"F0.wireOp",EDGE,"E140"),sQuery(id+"F0.wireOp",EDGE,"E141"),sQuery(id+"F0.wireOp",EDGE,"E142"),sQuery(id+"F0.wireOp",EDGE,"E143"),sQuery(id+"F0.wireOp",EDGE,"E144"),sQuery(id+"F0.wireOp",EDGE,"E145"),sQuery(id+"F0.wireOp",EDGE,"E146"),sQuery(id+"F0.wireOp",EDGE,"E147"),sQuery(id+"F0.wireOp",EDGE,"E148"),sQuery(id+"F0.wireOp",EDGE,"E149"),sQuery(id+"F0.wireOp",EDGE,"E150"),sQuery(id+"F0.wireOp",EDGE,"E151"),sQuery(id+"F0.wireOp",EDGE,"E152"),sQuery(id+"F0.wireOp",EDGE,"E153"),sQuery(id+"F0.wireOp",EDGE,"E154"),sQuery(id+"F0.wireOp",EDGE,"E155"),sQuery(id+"F0.wireOp",EDGE,"E156"),sQuery(id+"F0.wireOp",EDGE,"E157"),sQuery(id+"F0.wireOp",EDGE,"E158"),sQuery(id+"F0.wireOp",EDGE,"E159"),sQuery(id+"F0.wireOp",EDGE,"E160"),sQuery(id+"F0.wireOp",EDGE,"E161"),sQuery(id+"F0.wireOp",EDGE,"E162"),sQuery(id+"F0.wireOp",EDGE,"E163"),sQuery(id+"F0.wireOp",EDGE,"E164"),sQuery(id+"F0.wireOp",EDGE,"E165"),sQuery(id+"F0.wireOp",EDGE,"E166"),sQuery(id+"F0.wireOp",EDGE,"E167"),sQuery(id+"F0.wireOp",EDGE,"E168"),sQuery(id+"F0.wireOp",EDGE,"E169"),sQuery(id+"F0.wireOp",EDGE,"E170"),sQuery(id+"F0.wireOp",EDGE,"E171"),sQuery(id+"F0.wireOp",EDGE,"E172"),sQuery(id+"F0.wireOp",EDGE,"E173"),sQuery(id+"F0.wireOp",EDGE,"E174"),sQuery(id+"F0.wireOp",EDGE,"E175"),sQuery(id+"F0.wireOp",EDGE,"E176"),sQuery(id+"F0.wireOp",EDGE,"E177"),sQuery(id+"F0.wireOp",EDGE,"E178"),sQuery(id+"F0.wireOp",EDGE,"E179"),sQuery(id+"F0.wireOp",EDGE,"E180"),sQuery(id+"F0.wireOp",EDGE,"E181"),sQuery(id+"F0.wireOp",EDGE,"E182"),sQuery(id+"F0.wireOp",EDGE,"E183"),sQuery(id+"F0.wireOp",EDGE,"E184"),sQuery(id+"F0.wireOp",EDGE,"E185"),sQuery(id+"F0.wireOp",EDGE,"E186"),sQuery(id+"F0.wireOp",EDGE,"E187"),sQuery(id+"F0.wireOp",EDGE,"E188"),sQuery(id+"F0.wireOp",EDGE,"E189"),sQuery(id+"F0.wireOp",EDGE,"E190"),sQuery(id+"F0.wireOp",EDGE,"E191"),sQuery(id+"F0.wireOp",EDGE,"E192"),sQuery(id+"F0.wireOp",EDGE,"E193"),sQuery(id+"F0.wireOp",EDGE,"E194"),sQuery(id+"F0.wireOp",EDGE,"E195"),sQuery(id+"F0.wireOp",EDGE,"E196"),sQuery(id+"F0.wireOp",EDGE,"E197"),sQuery(id+"F0.wireOp",EDGE,"E198"),sQuery(id+"F0.wireOp",EDGE,"E199"),sQuery(id+"F0.wireOp",EDGE,"E200"),sQuery(id+"F0.wireOp",EDGE,"E201"),sQuery(id+"F0.wireOp",EDGE,"E202"),sQuery(id+"F0.wireOp",EDGE,"E203"),sQuery(id+"F0.wireOp",EDGE,"E204"),sQuery(id+"F0.wireOp",EDGE,"E205"),sQuery(id+"F0.wireOp",EDGE,"E206"),sQuery(id+"F0.wireOp",EDGE,"E207"),sQuery(id+"F0.wireOp",EDGE,"E208"),sQuery(id+"F0.wireOp",EDGE,"E209")])],"isStart":false});
            var sketch = newSketch(context, id + "F2", { "sketchPlane" : qUnion([Q0])});
            skArc(sketch, "E210", {"start": v(4.5, 0) * mm, "mid": v(0, 4.5) * mm, "end": v(-4.5, 0) * mm, "construction": true});
            skCircle(sketch, "E211", {"center": v(7.2, 6.2) * mm, "radius": 1.1 * mm});
            skCircle(sketch, "E212.MirrorC", {"center": v(-7.2, 6.2) * mm, "radius": 1.1 * mm, "construction": true});
            skLineSegment(sketch, "E213", {"start": v(-11.82, -3.69) * mm, "end": v(-4.5, -3.69) * mm, "construction": true});
            skLineSegment(sketch, "E214", {"start": v(-4.5, 0) * mm, "end": v(-4.5, -3.69) * mm, "construction": true});
            skLineSegment(sketch, "E215.MirrorCS", {"start": v(4.5, 0) * mm, "end": v(4.5, -3.69) * mm, "construction": true});
            skLineSegment(sketch, "E216.trimOffspring", {"start": v(4.5, -3.69) * mm, "end": v(12.57, -3.69) * mm, "construction": true});
            skLineSegment(sketch, "E217", {"start": v(12.57, -1.12) * mm, "end": v(12.57, -3.69) * mm});
            skCircle(sketch, "E218", {"center": v(-7.2, 6.45) * mm, "radius": 1.1 * mm});
            skLineSegment(sketch, "E219", {"start": v(7.2, 6.2) * mm, "end": v(-7.2, 6.45) * mm, "construction": true});
            skLineSegment(sketch, "E220", {"start": v(12.57, -3.69) * mm, "end": v(4.5, -3.54) * mm});
            skLineSegment(sketch, "E221.trimOffspring", {"start": v(-4.67, -3.39) * mm, "end": v(-11.93, -3.26) * mm});
            skPoint(sketch, "E222", {"position": v(0, 6.33) * mm});
            skLineSegment(sketch, "E223", {"start": v(0, 6.33) * mm, "end": v(-0.1, 0.13) * mm, "construction": true});
            skArc(sketch, "E224", {"start": v(4.4, 0.05) * mm, "mid": v(-0.56, 4.6) * mm, "end": v(-4.5, -0.85) * mm});
            skLineSegment(sketch, "E225", {"start": v(-0.1, 0.13) * mm, "end": v(-4.6, 0.2) * mm, "construction": true});
            skLineSegment(sketch, "E226", {"start": v(-0.1, 0.13) * mm, "end": v(4.4, 0.05) * mm, "construction": true});
            skLineSegment(sketch, "E227", {"start": v(-4.6, 0.2) * mm, "end": v(-4.67, -3.39) * mm});
            skLineSegment(sketch, "E228", {"start": v(4.4, 0.05) * mm, "end": v(4.33, -3.54) * mm});
            skLineSegment(sketch, "E229", {"start": v(4.5, -3.54) * mm, "end": v(4.33, -3.54) * mm});
            skSolve(sketch);
        }
        {
            var Q0;
            Q0=makeQuery(id+"F2.imprint","IMPRINT",FACE,{"disambiguationData":[TD([[makeQuery(id+"F2.imprint","IMPRINT",EDGE,{"derivedFrom":sQuery(id+"F2.wireOp",EDGE,"E218")}),1.0]])]});
            var Q1;
            Q1=makeQuery(id+"F2.imprint","IMPRINT",FACE,{"disambiguationData":[TD([[makeQuery(id+"F2.imprint","IMPRINT",EDGE,{"derivedFrom":sQuery(id+"F2.wireOp",EDGE,"E211")}),1.0]])]});
            var Q2;
            Q2=makeQuery(id+"F2.imprint","IMPRINT",FACE,{"disambiguationData":[TD([[makeQuery(id+"F2.imprint","IMPRINT",EDGE,{"derivedFrom":sQuery(id+"F2.wireOp",EDGE,"E217")}),1.0]])]});
            extrude(context, id + "F3", {"entities" : qUnion([Q0, Q1, Q2]), "operationType" : NewBodyOperationType.REMOVE, "endBound" : BoundingType.UP_TO_NEXT, "oppositeDirection" : true, "depth" : 25 * mm});
        }
        {
            var Q0;
            Q0=makeQuery(id+"F3.boolean.opBoolean","COPY",FACE,{"derivedFrom":makeQuery(id+"F3.opExtrude","SWEPT_FACE",FACE,{"disambiguationData":[OSD([sQuery(id+"F2.wireOp",EDGE,"E221.trimOffspring")])]})});
            var sketch = newSketch(context, id + "F4", { "sketchPlane" : qUnion([Q0])});
            skLineSegment(sketch, "E230.bottom", {"start": v(-11.87, 1.5) * mm, "end": v(-8.87, 1.5) * mm});
            skLineSegment(sketch, "E230.top", {"start": v(-11.87, 0) * mm, "end": v(-8.87, 0) * mm});
            skLineSegment(sketch, "E230.left", {"start": v(-11.87, 1.5) * mm, "end": v(-11.87, 0) * mm});
            skLineSegment(sketch, "E230.right", {"start": v(-8.87, 1.5) * mm, "end": v(-8.87, 0) * mm});
            skLineSegment(sketch, "E231.0", {"start": v(12.64, 1.5) * mm, "end": v(12.64, 1.5) * mm});
            skLineSegment(sketch, "E232.0", {"start": v(12.64, 0) * mm, "end": v(12.64, 1.5) * mm});
            skLineSegment(sketch, "E233.0", {"start": v(12.64, 0) * mm, "end": v(12.64, 0) * mm});
            skLineSegment(sketch, "E234", {"start": v(9.64, 1.5) * mm, "end": v(9.64, 0) * mm});
            skLineSegment(sketch, "E235.0", {"start": v(4.4, 0) * mm, "end": v(4.4, 1.5) * mm});
            skLineSegment(sketch, "E236", {"start": v(4.4, 1.5) * mm, "end": v(9.64, 1.5) * mm});
            skLineSegment(sketch, "E237", {"start": v(4.4, 0) * mm, "end": v(9.64, 0) * mm});
            skSolve(sketch);
        }
        {
            var Q0;
            {var subQ0=sQuery(id+"F4.wireOp",EDGE,"E232.0");Q0=makeQuery(id+"F4.imprint","IMPRINT",FACE,{"disambiguationData":[TD([[makeQuery(id+"F4.imprint","IMPRINT",EDGE,{"derivedFrom":subQ0}),1.0]])]});}
            var Q1;
            {var subQ0=sQuery(id+"F4.wireOp",EDGE,"E232.0");Q1=makeQuery(id+"F4.imprint","IMPRINT",FACE,{"disambiguationData":[TD([[makeQuery(id+"F4.imprint","IMPRINT",EDGE,{"derivedFrom":subQ0}),1.0]])]});}
            var Q2;
            {var subQ0=sQuery(id+"F4.wireOp",EDGE,"E230.right");Q2=makeQuery(id+"F4.imprint","IMPRINT",FACE,{"disambiguationData":[TD([[makeQuery(id+"F4.imprint","IMPRINT",EDGE,{"derivedFrom":subQ0}),1.0]])]});}
            var Q3;
            Q3=makeQuery(id+"F4.imprint","IMPRINT",FACE,{"disambiguationData":[TD([[makeQuery(id+"F4.imprint","IMPRINT",EDGE,{"derivedFrom":sQuery(id+"F4.wireOp",EDGE,"E230.bottom")}),1.0]])]});
            var Q4;
            Q4=makeQuery(id+"F4.imprint","IMPRINT",FACE,{"disambiguationData":[TD([[makeQuery(id+"F4.imprint","IMPRINT",EDGE,{"derivedFrom":sQuery(id+"F4.wireOp",EDGE,"E234")}),-1.0]])]});
            var Q5;
            Q5=makeQuery(id+"F3.boolean.opBoolean","COPY",FACE,{"derivedFrom":makeQuery(id+"F3.opExtrude","SWEPT_FACE",FACE,{"disambiguationData":[OSD([sQuery(id+"F2.wireOp",EDGE,"E220")])]})});
            extrude(context, id + "F5", {"entities" : qUnion([Q0, Q1, Q2, Q3, Q4, Q5]), "operationType" : NewBodyOperationType.ADD, "depth" : 3.3 * mm});
        }
    });
